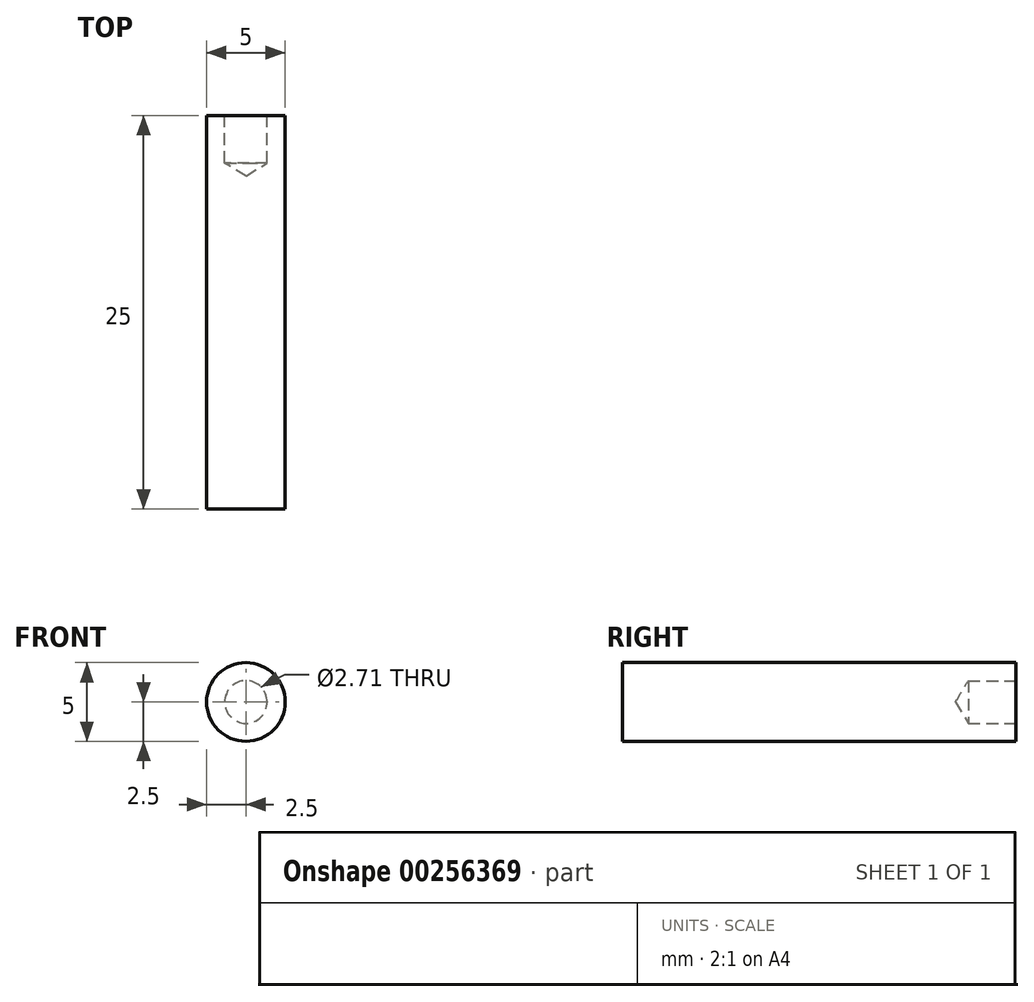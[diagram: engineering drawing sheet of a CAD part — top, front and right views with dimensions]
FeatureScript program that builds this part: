
annotation { "Feature Type Name" : "Feature", "Feature Type Description" : "" }
export const myFeature = defineFeature(function(context is Context, id is Id, definition is map)
    precondition{}
    {
        {
            var Q0;
            Q0=qCreatedBy(makeId("Front.planeOp"),FACE);
            var sketch = newSketch(context, id + "F0", { "sketchPlane" : qUnion([Q0])});
            skCircle(sketch, "E0", {"center": v(0, 0) * mm, "radius": 2.5 * mm});
            skSolve(sketch);
        }
        {
            var Q0;
            Q0 = qSketchRegion(id + "F0", true);
            extrude(context, id + "F1", {"entities" : qUnion([Q0]), "depth" : 25 * mm});
        }
        {
            var Q0;
            Q0=makeQuery(id+"F1.opExtrude","CAP_FACE",FACE,{"disambiguationData":[OSD([sQuery(id+"F0.wireOp",EDGE,"E0")])],"isStart":true});
            var sketch = newSketch(context, id + "F2", { "sketchPlane" : qUnion([Q0])});
            skPoint(sketch, "E1", {"position": v(0, 0) * mm});
            skCircle(sketch, "E2", {"center": v(0, 0) * mm, "radius": 1.99 * mm});
            skSolve(sketch);
        }
        {
            var Q0;
            Q0=sQuery(id+"F2.wireOp",VERTEX,"E1");
            var Q1;
            Q1=makeQuery(id+"F1.opExtrude","SWEPT_BODY",BODY,{"disambiguationData":[OSD([sQuery(id+"F0.wireOp",EDGE,"E0")])]});
            hole(context, id + "F3", {"style" : HoleStyle.SIMPLE, "endStyle" : HoleEndStyle.BLIND, "standardTappedOrClearance" : lookupTablePath({ "standard" : "ANSI", "engagement" : "75%", "pitch" : "32 tpi", "size" : "#6", "type" : "Tapped" }), "standardBlindInLast" : lookupTablePath({ "standard" : "ANSI", "engagement" : "75%", "pitch" : "32 tpi", "size" : "#6", "type" : "Tapped" }), "holeDiameter" : 2.7 * mm, "showTappedDepth" : true, "holeDepth" : 3.02 * mm, "tappedDepth" : 0.64 * mm, "tapClearance" : 3, "locations" : qUnion([Q0]), "scope" : qUnion([Q1]), "majorDiameter" : 3.5 * mm});
        }
    });
